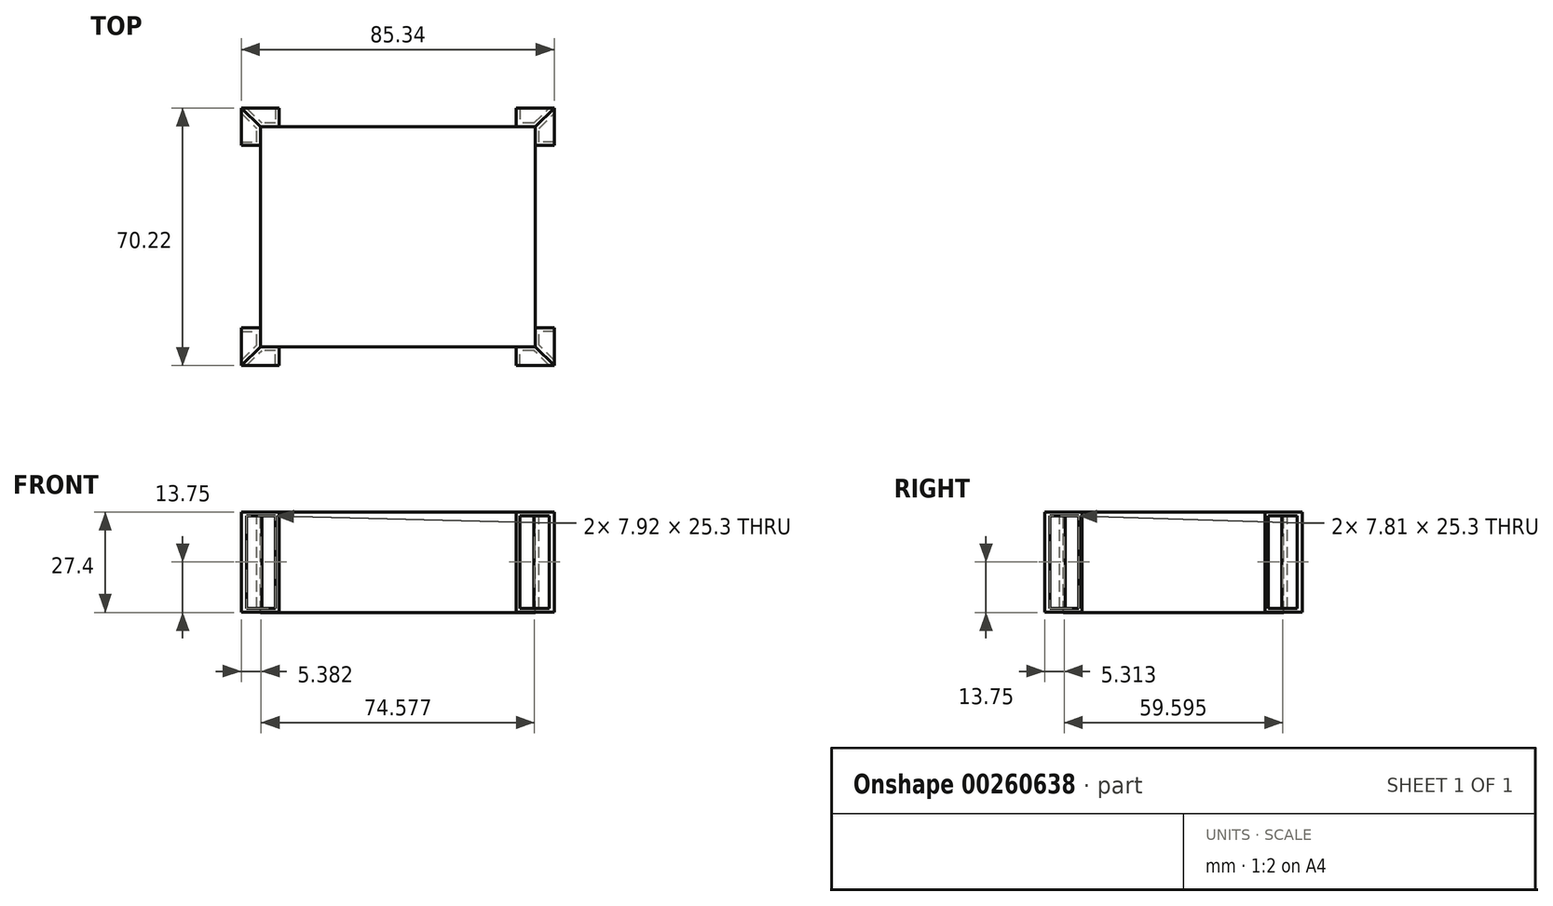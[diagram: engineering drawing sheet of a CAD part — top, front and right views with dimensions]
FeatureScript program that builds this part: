
annotation { "Feature Type Name" : "Feature", "Feature Type Description" : "" }
export const myFeature = defineFeature(function(context is Context, id is Id, definition is map)
    precondition{}
    {
        {
            var Q0;
            Q0=qCreatedBy(makeId("Top.planeOp"),FACE);
            var sketch = newSketch(context, id + "F0", { "sketchPlane" : qUnion([Q0])});
            skLineSegment(sketch, "E0.bottom", {"start": v(37.5, -30) * mm, "end": v(-37.5, -30) * mm});
            skLineSegment(sketch, "E0.top", {"start": v(37.5, 30) * mm, "end": v(-37.5, 30) * mm});
            skLineSegment(sketch, "E0.left", {"start": v(37.5, -30) * mm, "end": v(37.5, 30) * mm});
            skLineSegment(sketch, "E0.right", {"start": v(-37.5, -30) * mm, "end": v(-37.5, 30) * mm});
            skPoint(sketch, "E0.middle", {"position": v(0, 0) * mm});
            skLineSegment(sketch, "E1.bottom", {"start": v(-42.67, 35.1) * mm, "end": v(-32.33, 35.1) * mm});
            skLineSegment(sketch, "E1.top", {"start": v(-42.67, 24.9) * mm, "end": v(-32.33, 24.9) * mm});
            skLineSegment(sketch, "E1.left", {"start": v(-42.67, 35.1) * mm, "end": v(-42.67, 24.9) * mm});
            skLineSegment(sketch, "E1.right", {"start": v(-32.33, 35.1) * mm, "end": v(-32.33, 24.9) * mm});
            skPoint(sketch, "E1.middle", {"position": v(-37.5, 30) * mm});
            skLineSegment(sketch, "E2.MirrorCS", {"start": v(32.33, 35.1) * mm, "end": v(32.33, 24.9) * mm});
            skLineSegment(sketch, "E3.MirrorCS", {"start": v(42.67, 35.1) * mm, "end": v(42.67, 24.9) * mm});
            skLineSegment(sketch, "E4.MirrorCS", {"start": v(42.67, 24.9) * mm, "end": v(32.33, 24.9) * mm});
            skLineSegment(sketch, "E5.MirrorCS", {"start": v(42.67, 35.1) * mm, "end": v(32.33, 35.1) * mm});
            skLineSegment(sketch, "E6.MirrorCS", {"start": v(32.33, -35.1) * mm, "end": v(32.33, -24.9) * mm});
            skLineSegment(sketch, "E7.MirrorCS", {"start": v(42.67, -35.1) * mm, "end": v(32.33, -35.1) * mm});
            skLineSegment(sketch, "E8.MirrorCS", {"start": v(42.67, -35.1) * mm, "end": v(42.67, -24.9) * mm});
            skLineSegment(sketch, "E9.MirrorCS", {"start": v(42.67, -24.9) * mm, "end": v(32.33, -24.9) * mm});
            skLineSegment(sketch, "E10.MirrorCS", {"start": v(-32.33, -35.1) * mm, "end": v(-32.33, -24.9) * mm});
            skLineSegment(sketch, "E11.MirrorCS", {"start": v(-42.67, -35.1) * mm, "end": v(-32.33, -35.1) * mm});
            skLineSegment(sketch, "E12.MirrorCS", {"start": v(-42.67, -35.1) * mm, "end": v(-42.67, -24.9) * mm});
            skLineSegment(sketch, "E13.MirrorCS", {"start": v(-42.67, -24.9) * mm, "end": v(-32.33, -24.9) * mm});
            skLineSegment(sketch, "E14", {"start": v(-42.67, 35.1) * mm, "end": v(-37.5, 30) * mm});
            skLineSegment(sketch, "E15", {"start": v(37.5, 30) * mm, "end": v(42.67, 35.1) * mm});
            skLineSegment(sketch, "E16", {"start": v(42.67, -35.1) * mm, "end": v(37.5, -30) * mm});
            skLineSegment(sketch, "E17", {"start": v(-42.67, -35.1) * mm, "end": v(-37.5, -30) * mm});
            skSolve(sketch);
        }
        {
            var Q0;
            {var subQ1=sQuery(id+"F0.wireOp",EDGE,"E6.MirrorCS");var subQ19=sQuery(id+"F0.wireOp",EDGE,"E0.bottom");var subQ20=makeQuery(id+"F0.imprint","INTERSECT",VERTEX,{"derivedFrom":[subQ19,subQ1]});Q0=makeQuery(id+"F0.imprint","IMPRINT",FACE,{"disambiguationData":[TD([[makeQuery(id+"F0.imprint","IMPRINT",EDGE,{"disambiguationData":[TD([[subQ20,-1.0]])],"derivedFrom":subQ19}),-1.0]])]});}
            var Q1;
            {var subQ0=sQuery(id+"F0.wireOp",EDGE,"E0.right");var subQ1=sQuery(id+"F0.wireOp",EDGE,"E0.top");var subQ2=makeQuery(id+"F0.imprint","INTERSECT",VERTEX,{"derivedFrom":[subQ1,subQ0]});Q1=makeQuery(id+"F0.imprint","IMPRINT",FACE,{"disambiguationData":[TD([[makeQuery(id+"F0.imprint","IMPRINT",EDGE,{"disambiguationData":[TD([[subQ2,1.0]])],"derivedFrom":subQ1}),1.0]])]});}
            var Q2;
            {var subQ0=sQuery(id+"F0.wireOp",EDGE,"E0.left");var subQ1=sQuery(id+"F0.wireOp",EDGE,"E0.top");var subQ2=makeQuery(id+"F0.imprint","INTERSECT",VERTEX,{"derivedFrom":[subQ1,subQ0]});Q2=makeQuery(id+"F0.imprint","IMPRINT",FACE,{"disambiguationData":[TD([[makeQuery(id+"F0.imprint","IMPRINT",EDGE,{"disambiguationData":[TD([[subQ2,-1.0]])],"derivedFrom":subQ1}),1.0]])]});}
            var Q3;
            {var subQ0=sQuery(id+"F0.wireOp",EDGE,"E0.left");var subQ1=sQuery(id+"F0.wireOp",EDGE,"E0.bottom");var subQ2=makeQuery(id+"F0.imprint","INTERSECT",VERTEX,{"derivedFrom":[subQ1,subQ0]});Q3=makeQuery(id+"F0.imprint","IMPRINT",FACE,{"disambiguationData":[TD([[makeQuery(id+"F0.imprint","IMPRINT",EDGE,{"disambiguationData":[TD([[subQ2,-1.0]])],"derivedFrom":subQ1}),-1.0]])]});}
            var Q4;
            {var subQ0=sQuery(id+"F0.wireOp",EDGE,"E0.right");var subQ1=sQuery(id+"F0.wireOp",EDGE,"E0.bottom");var subQ2=makeQuery(id+"F0.imprint","INTERSECT",VERTEX,{"derivedFrom":[subQ1,subQ0]});Q4=makeQuery(id+"F0.imprint","IMPRINT",FACE,{"disambiguationData":[TD([[makeQuery(id+"F0.imprint","IMPRINT",EDGE,{"disambiguationData":[TD([[subQ2,1.0]])],"derivedFrom":subQ1}),-1.0]])]});}
            extrude(context, id + "F1", {"entities" : qUnion([Q0, Q1, Q2, Q3, Q4]), "oppositeDirection" : true, "depth" : 27.4 * mm});
        }
        {
            var Q0;
            {var subQ4=sQuery(id+"F0.wireOp",EDGE,"E1.left");Q0=makeQuery(id+"F0.imprint","IMPRINT",FACE,{"disambiguationData":[TD([[makeQuery(id+"F0.imprint","IMPRINT",EDGE,{"derivedFrom":subQ4}),1.0]])]});}
            var Q1;
            {var subQ4=sQuery(id+"F0.wireOp",EDGE,"E5.MirrorCS");Q1=makeQuery(id+"F0.imprint","IMPRINT",FACE,{"disambiguationData":[TD([[makeQuery(id+"F0.imprint","IMPRINT",EDGE,{"derivedFrom":subQ4}),1.0]])]});}
            var Q2;
            {var subQ4=sQuery(id+"F0.wireOp",EDGE,"E8.MirrorCS");Q2=makeQuery(id+"F0.imprint","IMPRINT",FACE,{"disambiguationData":[TD([[makeQuery(id+"F0.imprint","IMPRINT",EDGE,{"derivedFrom":subQ4}),1.0]])]});}
            var Q3;
            {var subQ4=sQuery(id+"F0.wireOp",EDGE,"E12.MirrorCS");Q3=makeQuery(id+"F0.imprint","IMPRINT",FACE,{"disambiguationData":[TD([[makeQuery(id+"F0.imprint","IMPRINT",EDGE,{"derivedFrom":subQ4}),-1.0]])]});}
            extrude(context, id + "F2", {"entities" : qUnion([Q0, Q1, Q2, Q3]), "oppositeDirection" : true, "depth" : 27.3 * mm});
        }
        {
            var Q0;
            {var subQ4=sQuery(id+"F0.wireOp",EDGE,"E1.bottom");Q0=makeQuery(id+"F0.imprint","IMPRINT",FACE,{"disambiguationData":[TD([[makeQuery(id+"F0.imprint","IMPRINT",EDGE,{"derivedFrom":subQ4}),-1.0]])]});}
            var Q1;
            {var subQ4=sQuery(id+"F0.wireOp",EDGE,"E3.MirrorCS");Q1=makeQuery(id+"F0.imprint","IMPRINT",FACE,{"disambiguationData":[TD([[makeQuery(id+"F0.imprint","IMPRINT",EDGE,{"derivedFrom":subQ4}),-1.0]])]});}
            var Q2;
            {var subQ4=sQuery(id+"F0.wireOp",EDGE,"E7.MirrorCS");Q2=makeQuery(id+"F0.imprint","IMPRINT",FACE,{"disambiguationData":[TD([[makeQuery(id+"F0.imprint","IMPRINT",EDGE,{"derivedFrom":subQ4}),-1.0]])]});}
            var Q3;
            {var subQ4=sQuery(id+"F0.wireOp",EDGE,"E11.MirrorCS");Q3=makeQuery(id+"F0.imprint","IMPRINT",FACE,{"disambiguationData":[TD([[makeQuery(id+"F0.imprint","IMPRINT",EDGE,{"derivedFrom":subQ4}),1.0]])]});}
            extrude(context, id + "F3", {"entities" : qUnion([Q0, Q1, Q2, Q3]), "oppositeDirection" : true, "depth" : 27.3 * mm});
        }
        {
            var Q0;
            Q0=makeQuery(id+"F2.opExtrude","SWEPT_FACE",FACE,{"disambiguationData":[OSD([sQuery(id+"F0.wireOp",EDGE,"E8.MirrorCS")])]});
            var Q1;
            Q1=makeQuery(id+"F3.opExtrude","SWEPT_FACE",FACE,{"disambiguationData":[OSD([sQuery(id+"F0.wireOp",EDGE,"E3.MirrorCS")])]});
            var Q2;
            Q2=makeQuery(id+"F2.opExtrude","SWEPT_FACE",FACE,{"disambiguationData":[OSD([sQuery(id+"F0.wireOp",EDGE,"E5.MirrorCS")])]});
            var Q3;
            Q3=makeQuery(id+"F3.opExtrude","SWEPT_FACE",FACE,{"disambiguationData":[OSD([sQuery(id+"F0.wireOp",EDGE,"E1.bottom")])]});
            var Q4;
            Q4=makeQuery(id+"F2.opExtrude","SWEPT_FACE",FACE,{"disambiguationData":[OSD([sQuery(id+"F0.wireOp",EDGE,"E12.MirrorCS")])]});
            var Q5;
            Q5=makeQuery(id+"F3.opExtrude","SWEPT_FACE",FACE,{"disambiguationData":[OSD([sQuery(id+"F0.wireOp",EDGE,"E11.MirrorCS")])]});
            var Q6;
            Q6=makeQuery(id+"F2.opExtrude","SWEPT_FACE",FACE,{"disambiguationData":[OSD([sQuery(id+"F0.wireOp",EDGE,"E1.left")])]});
            var Q7;
            Q7=makeQuery(id+"F3.opExtrude","SWEPT_FACE",FACE,{"disambiguationData":[OSD([sQuery(id+"F0.wireOp",EDGE,"E7.MirrorCS")])]});
            shell(context, id + "F4", {"entities" : qUnion([Q0, Q1, Q2, Q3, Q4, Q5, Q6, Q7]), "thickness" : 1 * mm});
        }
        {
            var Q0;
            Q0=makeQuery(id+"F1.opExtrude","CAP_FACE",FACE,{"disambiguationData":[OSD([sQuery(id+"F0.wireOp",EDGE,"E0.bottom"),sQuery(id+"F0.wireOp",EDGE,"E0.top"),sQuery(id+"F0.wireOp",EDGE,"E0.left"),sQuery(id+"F0.wireOp",EDGE,"E0.right")])],"isStart":false});
            var sketch = newSketch(context, id + "F5", { "sketchPlane" : qUnion([Q0])});
            skLineSegment(sketch, "E18", {"start": v(-37.5, 30) * mm, "end": v(37.5, -30) * mm});
            skLineSegment(sketch, "E19", {"start": v(37.5, -30) * mm, "end": v(-37.5, 0) * mm});
            skLineSegment(sketch, "E20", {"start": v(37.5, 30) * mm, "end": v(-37.5, -30) * mm});
            skLineSegment(sketch, "E21", {"start": v(-37.5, -30) * mm, "end": v(37.5, 0) * mm});
            skLineSegment(sketch, "E22", {"start": v(37.5, 0) * mm, "end": v(0, 30) * mm});
            skLineSegment(sketch, "E23", {"start": v(-37.5, 0) * mm, "end": v(0, 30) * mm});
            skLineSegment(sketch, "E24", {"start": v(0, 0) * mm, "end": v(0, -15) * mm});
            skLineSegment(sketch, "E25", {"start": v(0, -15) * mm, "end": v(0, 30) * mm});
            skLineSegment(sketch, "E26", {"start": v(37.5, -30) * mm, "end": v(27.16, -4.14) * mm});
            skLineSegment(sketch, "E27", {"start": v(-37.5, -30) * mm, "end": v(-27.16, -4.14) * mm});
            skLineSegment(sketch, "E28", {"start": v(-27.16, -4.14) * mm, "end": v(0, 14.35) * mm});
            skLineSegment(sketch, "E29", {"start": v(0, 14.35) * mm, "end": v(27.16, -4.14) * mm});
            skSolve(sketch);
        }
        {
            var Q0;
            Q0=sQuery(id+"F5.wireOp",EDGE,"E23");
            var Q1;
            Q1=sQuery(id+"F5.wireOp",EDGE,"E22");
            var Q2;
            Q2=sQuery(id+"F5.wireOp",EDGE,"E29");
            var Q3;
            Q3=sQuery(id+"F5.wireOp",EDGE,"E28");
            var Q4;
            Q4=sQuery(id+"F5.wireOp",EDGE,"E27");
            var Q5;
            Q5=sQuery(id+"F5.wireOp",EDGE,"E26");
            extrude(context, id + "F6", {"bodyType" : ToolBodyType.SURFACE, "surfaceEntities" : qUnion([Q0, Q1, Q2, Q3, Q4, Q5]), "depth" : 1 * mm});
        }
        {
            var Q0;
            Q0=sQuery(id+"F5.wireOp",EDGE,"E21");
            var Q1;
            Q1=sQuery(id+"F5.wireOp",EDGE,"E20");
            extrude(context, id + "F7", {"bodyType" : ToolBodyType.SURFACE, "surfaceEntities" : qUnion([Q0, Q1]), "depth" : 1 * mm});
        }
        {
            var Q0;
            Q0=sQuery(id+"F5.wireOp",EDGE,"E18");
            var Q1;
            Q1=sQuery(id+"F5.wireOp",EDGE,"E19");
            extrude(context, id + "F8", {"bodyType" : ToolBodyType.SURFACE, "surfaceEntities" : qUnion([Q0, Q1]), "depth" : 1 * mm});
        }
    });
